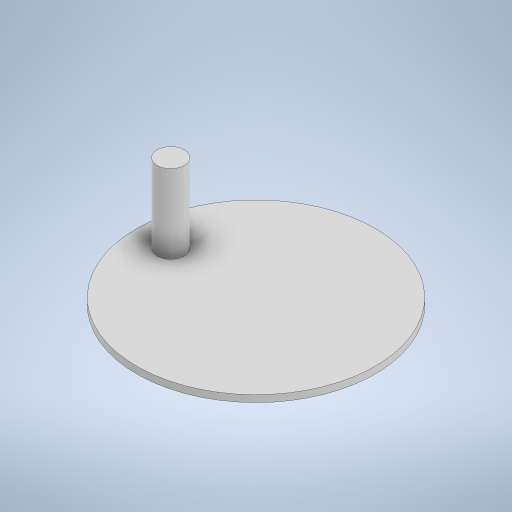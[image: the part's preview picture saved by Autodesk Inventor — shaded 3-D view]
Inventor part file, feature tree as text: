
AUTODESK INVENTOR PART (.ipt)
format: ipt  version: 2024.3 (Build 283343000, 343)  size: 221,696 bytes
history: native  units: mm
features: extrude x2, sketch x1
ambient origin geometry x8: Origin, YZ Plane, XZ Plane, XY Plane, X Axis, Y Axis, Z Axis, Center Point
bodies: Solid1 (feature_tree)
feature tree (3):
  sketch  "Sketch1"  dims[d0=70.0mm d1=8.0mm d2=25.0mm d3=2.0mm d4=0.0mm d5=25.0mm d6=0.0mm]
  extrude  "Extrusion1"  Depth=25.0mm
  extrude  "Extrusion2"  Depth=25.0mm
